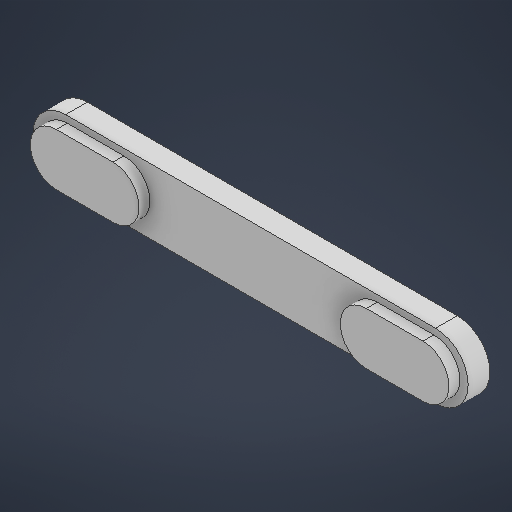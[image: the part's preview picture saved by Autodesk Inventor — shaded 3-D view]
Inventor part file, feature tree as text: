
AUTODESK INVENTOR PART (.ipt)
format: ipt  version: 2025 (Build 290162000, 162)  size: 217,600 bytes
history: native  units: mm
features: extrude x2, sketch x1
ambient origin geometry x8: Origin, YZ Plane, XZ Plane, XY Plane, X Axis, Y Axis, Z Axis, Center Point
bodies: 实体1 (feature_tree)
feature tree (3):
  sketch  "草图1"  dims[d0=20.0mm d1=3.0mm d2=5.0mm d3=1.0mm d4=0.0mm d5=1.5mm d6=0.0mm]
  extrude  "拉伸1"  Depth=3.0mm
  extrude  "拉伸2"  Depth=1.5mm
